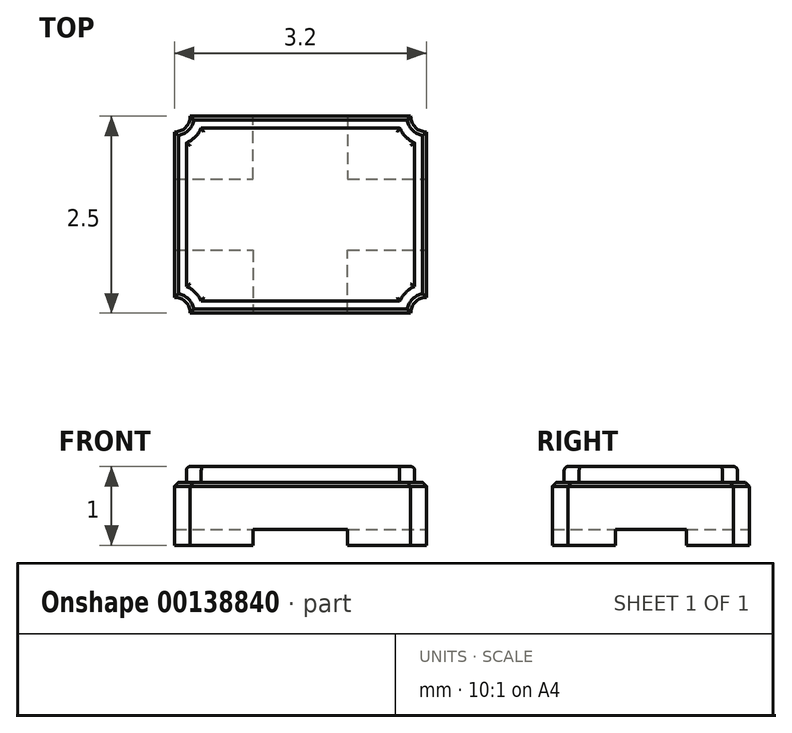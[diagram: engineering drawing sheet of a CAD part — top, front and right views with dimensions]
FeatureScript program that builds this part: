
annotation { "Feature Type Name" : "Feature", "Feature Type Description" : "" }
export const myFeature = defineFeature(function(context is Context, id is Id, definition is map)
    precondition{}
    {
        {
            var Q0;
            Q0=qCreatedBy(makeId("Top.planeOp"),FACE);
            var sketch = newSketch(context, id + "F0", { "sketchPlane" : qUnion([Q0])});
            skLineSegment(sketch, "E0.bottom", {"start": v(-1.4, 1.25) * mm, "end": v(1.4, 1.25) * mm});
            skLineSegment(sketch, "E0.top", {"start": v(-1.4, -1.25) * mm, "end": v(1.4, -1.25) * mm});
            skLineSegment(sketch, "E0.left", {"start": v(-1.6, 1.05) * mm, "end": v(-1.6, -1.05) * mm});
            skLineSegment(sketch, "E0.right", {"start": v(1.6, 1.05) * mm, "end": v(1.6, -1.05) * mm});
            skPoint(sketch, "E1.visualSharp", {"position": v(-1.6, 1.25) * mm});
            skPoint(sketch, "E2.visualSharp", {"position": v(1.6, 1.25) * mm});
            skPoint(sketch, "E3.visualSharp", {"position": v(1.6, -1.25) * mm});
            skPoint(sketch, "E4.visualSharp", {"position": v(-1.6, -1.25) * mm});
            skArc(sketch, "E5", {"start": v(-1.6, 1.05) * mm, "mid": v(-1.46, 1.1) * mm, "end": v(-1.4, 1.25) * mm});
            skArc(sketch, "E6", {"start": v(1.4, 1.25) * mm, "mid": v(1.46, 1.1) * mm, "end": v(1.6, 1.05) * mm});
            skArc(sketch, "E7", {"start": v(1.6, -1.05) * mm, "mid": v(1.46, -1.1) * mm, "end": v(1.4, -1.25) * mm});
            skArc(sketch, "E8", {"start": v(-1.4, -1.25) * mm, "mid": v(-1.46, -1.1) * mm, "end": v(-1.6, -1.05) * mm});
            skSolve(sketch);
        }
        {
            var Q0;
            Q0 = qSketchRegion(id + "F0", true);
            extrude(context, id + "F1", {"entities" : qUnion([Q0]), "depth" : .8 * mm});
        }
        {
            var Q0;
            Q0=makeQuery(id+"F1.opExtrude","CAP_FACE",FACE,{"disambiguationData":[OSD([sQuery(id+"F0.wireOp",EDGE,"E0.bottom"),sQuery(id+"F0.wireOp",EDGE,"E0.top"),sQuery(id+"F0.wireOp",EDGE,"E0.left"),sQuery(id+"F0.wireOp",EDGE,"E0.right"),sQuery(id+"F0.wireOp",EDGE,"E5"),sQuery(id+"F0.wireOp",EDGE,"E6"),sQuery(id+"F0.wireOp",EDGE,"E7"),sQuery(id+"F0.wireOp",EDGE,"E8")])],"isStart":false});
            var sketch = newSketch(context, id + "F2", { "sketchPlane" : qUnion([Q0])});
            skLineSegment(sketch, "E9", {"start": v(-1.26, 1.1) * mm, "end": v(1.26, 1.1) * mm});
            skLineSegment(sketch, "E10", {"start": v(1.45, 0.91) * mm, "end": v(1.45, -0.91) * mm});
            skLineSegment(sketch, "E11", {"start": v(1.26, -1.1) * mm, "end": v(-1.26, -1.1) * mm});
            skLineSegment(sketch, "E12", {"start": v(-1.45, -0.91) * mm, "end": v(-1.45, 0.91) * mm});
            skArc(sketch, "E13", {"start": v(-1.45, -0.91) * mm, "mid": v(-1.34, -0.99) * mm, "end": v(-1.26, -1.1) * mm});
            skArc(sketch, "E14", {"start": v(1.26, -1.1) * mm, "mid": v(1.34, -0.99) * mm, "end": v(1.45, -0.91) * mm});
            skArc(sketch, "E15", {"start": v(1.45, 0.91) * mm, "mid": v(1.34, 0.99) * mm, "end": v(1.26, 1.1) * mm});
            skArc(sketch, "E16", {"start": v(-1.45, 0.91) * mm, "mid": v(-1.34, 0.99) * mm, "end": v(-1.26, 1.1) * mm});
            skLineSegment(sketch, "E17", {"start": v(1.6, 0) * mm, "end": v(1.45, 0) * mm, "construction": true});
            skLineSegment(sketch, "E18", {"start": v(0, -1.25) * mm, "end": v(0, -1.1) * mm, "construction": true});
            skLineSegment(sketch, "E19", {"start": v(0, -1.1) * mm, "end": v(0, -1.1) * mm, "construction": true});
            skLineSegment(sketch, "E20", {"start": v(-1.6, 0) * mm, "end": v(-1.45, 0) * mm, "construction": true});
            skLineSegment(sketch, "E21", {"start": v(0, 1.25) * mm, "end": v(0, 1.1) * mm, "construction": true});
            skSolve(sketch);
        }
        {
            var Q0;
            Q0 = qSketchRegion(id + "F2", true);
            extrude(context, id + "F3", {"entities" : qUnion([Q0]), "depth" : .2 * mm});
        }
        {
            var Q0;
            Q0=makeQuery(id+"F1.opExtrude","CAP_EDGE",EDGE,{"disambiguationData":[OSD([sQuery(id+"F0.wireOp",EDGE,"E0.top")])],"isStart":false});
            var Q1;
            Q1=makeQuery(id+"F1.opExtrude","CAP_EDGE",EDGE,{"disambiguationData":[OSD([sQuery(id+"F0.wireOp",EDGE,"E8")])],"isStart":false});
            var Q2;
            Q2=makeQuery(id+"F1.opExtrude","CAP_EDGE",EDGE,{"disambiguationData":[OSD([sQuery(id+"F0.wireOp",EDGE,"E0.left")])],"isStart":false});
            var Q3;
            Q3=makeQuery(id+"F1.opExtrude","CAP_EDGE",EDGE,{"disambiguationData":[OSD([sQuery(id+"F0.wireOp",EDGE,"E7")])],"isStart":false});
            var Q4;
            Q4=makeQuery(id+"F1.opExtrude","CAP_EDGE",EDGE,{"disambiguationData":[OSD([sQuery(id+"F0.wireOp",EDGE,"E0.right")])],"isStart":false});
            var Q5;
            Q5=makeQuery(id+"F1.opExtrude","CAP_EDGE",EDGE,{"disambiguationData":[OSD([sQuery(id+"F0.wireOp",EDGE,"E6")])],"isStart":false});
            var Q6;
            Q6=makeQuery(id+"F1.opExtrude","CAP_EDGE",EDGE,{"disambiguationData":[OSD([sQuery(id+"F0.wireOp",EDGE,"E0.bottom")])],"isStart":false});
            var Q7;
            Q7=makeQuery(id+"F1.opExtrude","CAP_EDGE",EDGE,{"disambiguationData":[OSD([sQuery(id+"F0.wireOp",EDGE,"E5")])],"isStart":false});
            chamfer(context, id + "F4", {"entities" : qUnion([Q0, Q1, Q2, Q3, Q4, Q5, Q6, Q7]), "width" : 0.05 * mm, "tangentPropagation" : true});
        }
        {
            var Q0;
            Q0=makeQuery(id+"F3.opExtrude","CAP_EDGE",EDGE,{"disambiguationData":[OSD([sQuery(id+"F2.wireOp",EDGE,"E11")])],"isStart":false});
            var Q1;
            Q1=makeQuery(id+"F3.opExtrude","CAP_EDGE",EDGE,{"disambiguationData":[OSD([sQuery(id+"F2.wireOp",EDGE,"E13")])],"isStart":false});
            var Q2;
            Q2=makeQuery(id+"F3.opExtrude","CAP_FACE",FACE,{"disambiguationData":[OSD([sQuery(id+"F2.wireOp",EDGE,"E9"),sQuery(id+"F2.wireOp",EDGE,"E10"),sQuery(id+"F2.wireOp",EDGE,"E11"),sQuery(id+"F2.wireOp",EDGE,"E12"),sQuery(id+"F2.wireOp",EDGE,"E13"),sQuery(id+"F2.wireOp",EDGE,"E14"),sQuery(id+"F2.wireOp",EDGE,"E15"),sQuery(id+"F2.wireOp",EDGE,"E16")])],"isStart":false});
            var Q3;
            Q3=makeQuery(id+"F3.opExtrude","CAP_EDGE",EDGE,{"disambiguationData":[OSD([sQuery(id+"F2.wireOp",EDGE,"E14")])],"isStart":false});
            var Q4;
            Q4=makeQuery(id+"F3.opExtrude","CAP_EDGE",EDGE,{"disambiguationData":[OSD([sQuery(id+"F2.wireOp",EDGE,"E10")])],"isStart":false});
            var Q5;
            Q5=makeQuery(id+"F3.opExtrude","CAP_EDGE",EDGE,{"disambiguationData":[OSD([sQuery(id+"F2.wireOp",EDGE,"E15")])],"isStart":false});
            var Q6;
            Q6=makeQuery(id+"F3.opExtrude","CAP_EDGE",EDGE,{"disambiguationData":[OSD([sQuery(id+"F2.wireOp",EDGE,"E9")])],"isStart":false});
            var Q7;
            Q7=makeQuery(id+"F3.opExtrude","CAP_EDGE",EDGE,{"disambiguationData":[OSD([sQuery(id+"F2.wireOp",EDGE,"E16")])],"isStart":false});
            var Q8;
            Q8=makeQuery(id+"F3.opExtrude","CAP_EDGE",EDGE,{"disambiguationData":[OSD([sQuery(id+"F2.wireOp",EDGE,"E12")])],"isStart":false});
            fillet(context, id + "F5", {"entities" : qUnion([Q0, Q1, Q2, Q3, Q4, Q5, Q6, Q7, Q8]), "radius" : 0.05 * mm, "tangentPropagation" : true, "allowEdgeOverflow" : false});
        }
        {
            var Q0;
            Q0=makeQuery(id+"F1.opExtrude","CAP_FACE",FACE,{"disambiguationData":[OSD([sQuery(id+"F0.wireOp",EDGE,"E0.bottom"),sQuery(id+"F0.wireOp",EDGE,"E0.top"),sQuery(id+"F0.wireOp",EDGE,"E0.left"),sQuery(id+"F0.wireOp",EDGE,"E0.right"),sQuery(id+"F0.wireOp",EDGE,"E5"),sQuery(id+"F0.wireOp",EDGE,"E6"),sQuery(id+"F0.wireOp",EDGE,"E7"),sQuery(id+"F0.wireOp",EDGE,"E8")])],"isStart":true});
            var sketch = newSketch(context, id + "F6", { "sketchPlane" : qUnion([Q0])});
            skLineSegment(sketch, "E22", {"start": v(-1.6, 0.45) * mm, "end": v(-0.6, 0.45) * mm});
            skLineSegment(sketch, "E23", {"start": v(-0.6, 0.45) * mm, "end": v(-0.6, 1.25) * mm});
            skLineSegment(sketch, "E24", {"start": v(0.6, 1.25) * mm, "end": v(0.6, 0.45) * mm});
            skLineSegment(sketch, "E25", {"start": v(0.6, 0.45) * mm, "end": v(1.6, 0.45) * mm});
            skLineSegment(sketch, "E26", {"start": v(-1.6, -0.45) * mm, "end": v(-0.6, -0.45) * mm});
            skLineSegment(sketch, "E27", {"start": v(-0.6, -0.45) * mm, "end": v(-0.6, -1.25) * mm});
            skLineSegment(sketch, "E28", {"start": v(0.6, -1.25) * mm, "end": v(0.6, -0.45) * mm});
            skLineSegment(sketch, "E29", {"start": v(0.6, -0.45) * mm, "end": v(1.6, -0.45) * mm});
            skLineSegment(sketch, "E30", {"start": v(-1.6, 0.45) * mm, "end": v(-1.6, -0.45) * mm});
            skLineSegment(sketch, "E31", {"start": v(-0.6, -1.25) * mm, "end": v(0.6, -1.25) * mm});
            skLineSegment(sketch, "E32", {"start": v(1.6, -0.45) * mm, "end": v(1.6, 0.45) * mm});
            skLineSegment(sketch, "E33", {"start": v(0.6, 1.25) * mm, "end": v(-0.6, 1.25) * mm});
            skPoint(sketch, "E34.7.start.orphan", {"position": v(-1.4, 1.25) * mm});
            skPoint(sketch, "E35.trimOffspring.end.orphan", {"position": v(-1.6, 1.05) * mm});
            skPoint(sketch, "E34.1.end.orphan", {"position": v(1.4, 1.25) * mm});
            skPoint(sketch, "E36.trimOffspring.end.orphan", {"position": v(1.6, 1.05) * mm});
            skPoint(sketch, "E34.3.end.orphan", {"position": v(1.6, -1.05) * mm});
            skPoint(sketch, "E37.trimOffspring.end.orphan", {"position": v(1.4, -1.25) * mm});
            skPoint(sketch, "E34.5.end.orphan", {"position": v(-1.4, -1.25) * mm});
            skPoint(sketch, "E34.6.start.orphan", {"position": v(-1.6, -1.05) * mm});
            skSolve(sketch);
        }
        {
            var Q0;
            Q0 = qSketchRegion(id + "F6", true);
            extrude(context, id + "F7", {"entities" : qUnion([Q0]), "operationType" : NewBodyOperationType.REMOVE, "oppositeDirection" : true, "depth" : .2 * mm});
        }
    });
